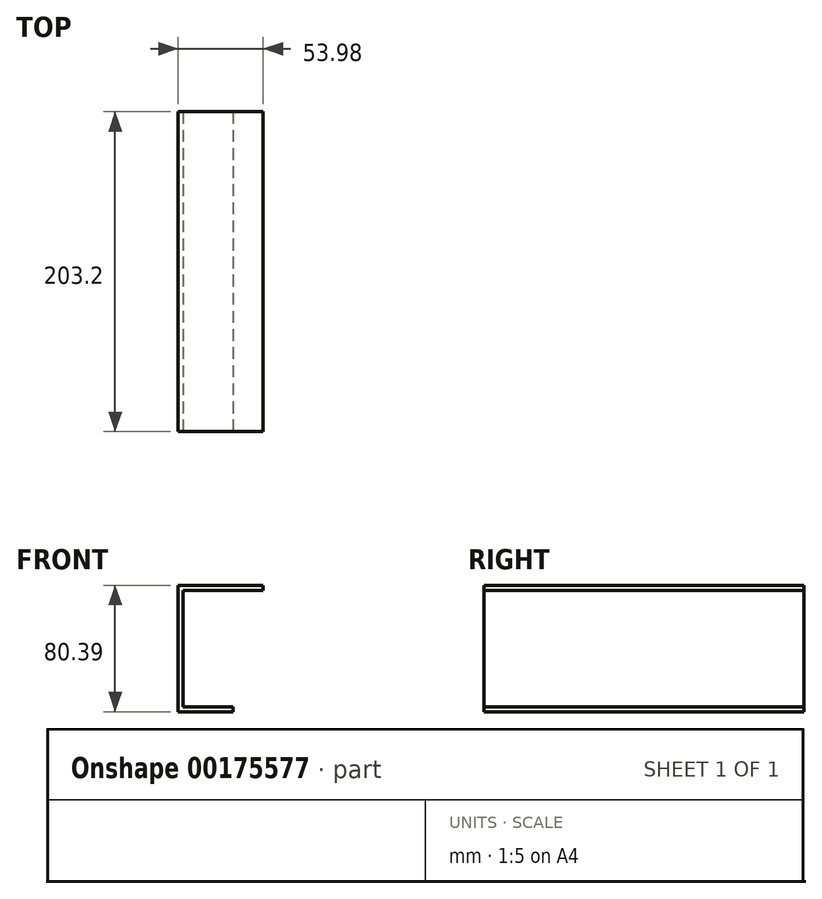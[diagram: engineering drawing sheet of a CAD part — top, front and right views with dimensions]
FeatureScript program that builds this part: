
annotation { "Feature Type Name" : "Feature", "Feature Type Description" : "" }
export const myFeature = defineFeature(function(context is Context, id is Id, definition is map)
    precondition{}
    {
        {
            var Q0;
            Q0=qCreatedBy(makeId("Front.planeOp"),FACE);
            var sketch = newSketch(context, id + "F0", { "sketchPlane" : qUnion([Q0])});
            skLineSegment(sketch, "E0", {"start": v(0, 45.18) * mm, "end": v(-53.98, 45.18) * mm});
            skLineSegment(sketch, "E1", {"start": v(-53.98, 45.18) * mm, "end": v(-53.98, -35.2) * mm});
            skLineSegment(sketch, "E2", {"start": v(-53.98, -35.2) * mm, "end": v(-19.05, -35.2) * mm});
            skLineSegment(sketch, "E3", {"start": v(-19.05, -35.2) * mm, "end": v(-19.05, -32.03) * mm});
            skLineSegment(sketch, "E4", {"start": v(-19.05, -32.03) * mm, "end": v(-50.8, -32.03) * mm});
            skLineSegment(sketch, "E5", {"start": v(-50.8, -32.03) * mm, "end": v(-50.8, 42) * mm});
            skLineSegment(sketch, "E6", {"start": v(-50.8, 42) * mm, "end": v(0, 42) * mm});
            skLineSegment(sketch, "E7", {"start": v(0, 42) * mm, "end": v(0, 45.18) * mm});
            skSolve(sketch);
        }
        {
            var Q0;
            Q0=makeQuery(id+"F0.imprint","IMPRINT",FACE,{"disambiguationData":[TD([[makeQuery(id+"F0.imprint","IMPRINT",EDGE,{"derivedFrom":sQuery(id+"F0.wireOp",EDGE,"E0")}),1.0]])]});
            extrude(context, id + "F1", {"entities" : qUnion([Q0]), "oppositeDirection" : true, "depth" : 203.2 * mm});
        }
    });
